# Revit family: VIESSMANN - Energycal AWH Pro AT 75-90
name_source: partatom
category: Wyposażenie mechaniczne
revit_build: Autodesk Revit 2017 (Build: 20160720_1515(x64)
units: mm (PartAtom-declared; Revit-internal decimal feet)

## family parameters
Numer OmniClass = 23.75.10.21.11
Oparty na płaszczyźnie roboczej = Nie
Punkt obliczania pomieszczeń = Nie
Tnij formami wycięć po wczytaniu = Nie
Typ części = Normalny
Tytuł OmniClass = Air-Source Heat Pumps
Współdzielony = Nie
Wymiar okrągłego złącza = Użyj średnicy
Zawsze pionowo = Tak

## types (2) — shared parameters
Autor = www.archispace.pl
Częstotliwość = 50 Hz
Głębokość = 1208 mm  [stored 3.96325 ft]
Ilość/Obiegi chłodnicze sprężarki (nr/nr) = 1/1
Klasa energetyczna = A+
Liczba biegunów = 3
Liczba wentylatorów = 2
Moc nominalna wentylatora = 2 kW
Model = Powietrzna pompa ciepła Energycal AWH PRO AT / Air-water heat pump Energycal AWH PRO AT
Naczynie wzbiorcze = 18 m³
Napięcie zasilania = 400 V
Opis = Energycal AWH Pro AT to typoszereg wysokotemperaturowych pomp ciepła z czynnikiem chłodniczym R134a lub R513A osiągających na zasilaniu temperatury wody do 80°C.
Pojemność zbiornika buforowego = 250 m³
Poziom ciśnienia akustycznego - wersja cicha LN dB(A) = 57 mm  [stored 0.187008 ft]
Poziom ciśnienia akustycznego - wersja super cicha SLN dB(A) = 55 mm  [stored 0.180446 ft]
Poziom ciśnienia akustycznego dB(A) = 59 mm
Poziom mocy akustycznej - wersja cicha LN dB(A) = 89 mm  [stored 0.291995 ft]
Poziom mocy akustycznej - wersja super cicha SLN dB(A) = 87 mm  [stored 0.285433 ft]
Poziom mocy akustycznej dB(A) = 91 mm  [stored 0.298556 ft]
Połączenia hydrauliczne = 2"
Producent = Viessmann Sp. z o.o
Prąd nominalny wentylatora = 4 A
Stopień wydajności = 2
Strefa serwisowa_przód = 1000 mm  [stored 3.28084 ft]
Typ sprężarki = Reciprocating
Typ wentylatora = Osiowy
Typ wymiennika po stronie grzewczej = Plate exchanger
URL = https://www.viessmann-projektant.pl
Viessmann Kolor 1 = Viessmann Kolor 2
Viessmann Kolor 2 = Viessmann Kolor 3
Współczynnik efektywności [COP] (A7W45) = 3.33
Współczynnik mocy = 1
Wysokość = 1912 mm  [stored 6.27297 ft]
Zasilanie elektryczne (V/ph/Hz) = 400/3N~/50+5%
Zasilanie pomocnicze (V/ph/Hz) = 230/1~/50+5%

## per-type parameters (varying)
| type | Całkowite napełnienie czynnikiem chłodniczym | Całkowite napełnienie olejem | Ciśnienie podnoszenia pompy (A7W45) | Efektywność sezonowa ηs | Maksymalna moc pobierania | Maksymalny pobór prądu | Maksymalny prąd rozruchowy | Moc nominalna silnika pompy obiegowej | Natężenie przepływu wody (A7W45) | Natężenie przepływu wody (A7W45) l/h | Nominalna moc grzewcza (A7W45) | Nominalna moc pompy | Obciążenie pozorne | Pobór mocy elektrycznej (A7W45) | Przepływ powietrza | Prąd nominalny silnika pompy obiegowej | SCOP | Spadek ciśnienia wody (A7W45) | Strefa serwisowa_tył | Szerokość |
| Wielkość jednostki - 75 | 39.00 kg | 4.80 kg | 134.0 kPa | 110.7 | 43 kW | 84 A | 197 A | 1 kW | 3.7 L/s | 13381 | 78 kW | 1 kW | 43 kW | 24 kW | 38500.0 m³/h | 2 A | 2.84 | 34.0 kPa | 1000 mm  [stored 3.28084 ft] | 3510 mm  [stored 11.5157 ft] |
| Wielkość jednostki - 90 | 40.00 kg | 4.00 kg | 185.0 kPa | 111.6 | 48 kW | 102 A | 242 A | 2 kW | 4.2 L/s | 15030 | 88 kW | 2 kW | 48 kW | 26 kW | 40000.0 m³/h | 3 A | 2.86 | 20.0 kPa | 2000 mm  [stored 6.56168 ft] | 3508 mm  [stored 11.5092 ft] |

note: [stored X ft] marks values corroborated as IEEE doubles in the binary element streams (Revit-internal decimal feet)
